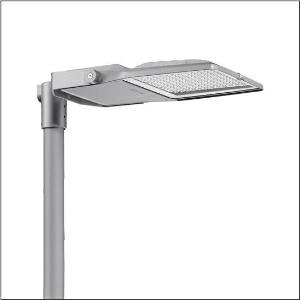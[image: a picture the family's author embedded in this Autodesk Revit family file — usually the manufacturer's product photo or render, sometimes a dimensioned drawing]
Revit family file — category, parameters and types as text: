
# Revit family: floodlight_fl_21_iq_midi___pl33t_5xa7782f2f3a_348f
name_source: partatom
category: Lighting Fixtures
units: mm (PartAtom-declared; Revit-internal decimal feet)

## family parameters
Cut with Voids When Loaded = No
Host = Face
Light Source = No
Part Type = Normal
Room Calculation Point = No
Round Connector Dimension = Use Diameter
Shared = No

## types (1)
- --- (1 x LED, 35350 lm, 270.2 W, 3000K)
    Apparent Load = 270 VA
    CIE Flux Codes = 26 75 99 100 100
    Color Rendering = 70
    Color Temperature = 3000K
    Default Elevation = 1800 mm
    Description = Floodlight FL 21 iQ midi, floodlight, primary light control with lens, of PMMA, primary optical cover: protective disc, of toughened safety glass, transparent, light distribution: PL33T, light emission: direct distribution, installation type: surface-mounted, LED, High Power LED, rated luminous flux: 35.350lm, luminous efficacy: 131lm/W, light colour: 730, colour temperature: 3000K, control gear: ECG iQ, control: optimised constant luminous flux control (CLO 2.0), Desk-Remote (wireless, voltage-free reading and setting of iQ features in the workshop via application-optimized NFC function/RFID function), Smart-Wire, Night-Set, Temp-Guard, Auto-Match, Street-Remote, with terminal, 6-pole, mains connection: 220..240V, AC, 50/60Hz, start of lifetime: 270W, end of service life: 287W, reduction: 117W, luminaire housing, of diecast aluminium, powder-coated, Siteco® metallic grey (DB 702S), corrosivity category C5 mid according to DIN EN ISO 12944, sealing non-destructively replaceable, please order mast flange separately, mast bracket, of steel, galvanised, powder-coated, Siteco® metallic grey (DB 702S), protection rating (complete): IP66, insulation class (complete): insulation class II (safety insulation), certification: CE, protection symbol: D, impact resistance: IK08, permissible operating ambient temperature: -40..+40°C, permissible operating ambient temperature for outdoor applications: -40..+50°C, standard: DIN EN 12944, LABS conformity tested according to VDMA 24364:2018-05, packaging unit: 1 piece

Light Distribution: PL33T
    Height = 76 mm
    Lamp = 1 x LED
    Lamp Light Flux = 35350 lm
    Lamp Power = 270.2 W
    Lamp count = 1
    Length = 657 mm
    Luminous efficacy = 131 lm/W
    Manufacturer = Siteco
    ModVariant = No
    Model = 5XA7782F2F3A
    Number of Poles = 1
    OnlyDefault = Yes
    Power Factor = 1
    Product Name = Floodlight FL 21 iQ midi | PL33T
    Product group = floodlight | pylon annexe
    ProductGroupID = 6200
    Protection Class = Protection class II
    Protection Degree = IP 66
    RLX_Detail_Level = 1
    RLX_Emergency_Light_Flux = 0 lm
    RLX_Emergency_Type = 0
    RLX_Emergency_Type_DB = No
    RlxData = <blob elided: 153253 chars, md5=4023f289>
    Socket = socket
    Standby Power = 0 W
    System Light Flux = 35350 lm
    System Power = 270 W
    Type Comments = factory setting: luminous flux: 100 % | dim-lin: 254 | 620 mA
    Type Image = l_1007123.jpg
    URL = http://relux.com
    VarID = @adj_051659
    Voltage = 0 V
    Weight = 0.00 kg
    Width = 442 mm

## geometry (parser evidence)
native form markers: Blend x4, Sweep x12
no freeform markers — native parametric forms only
